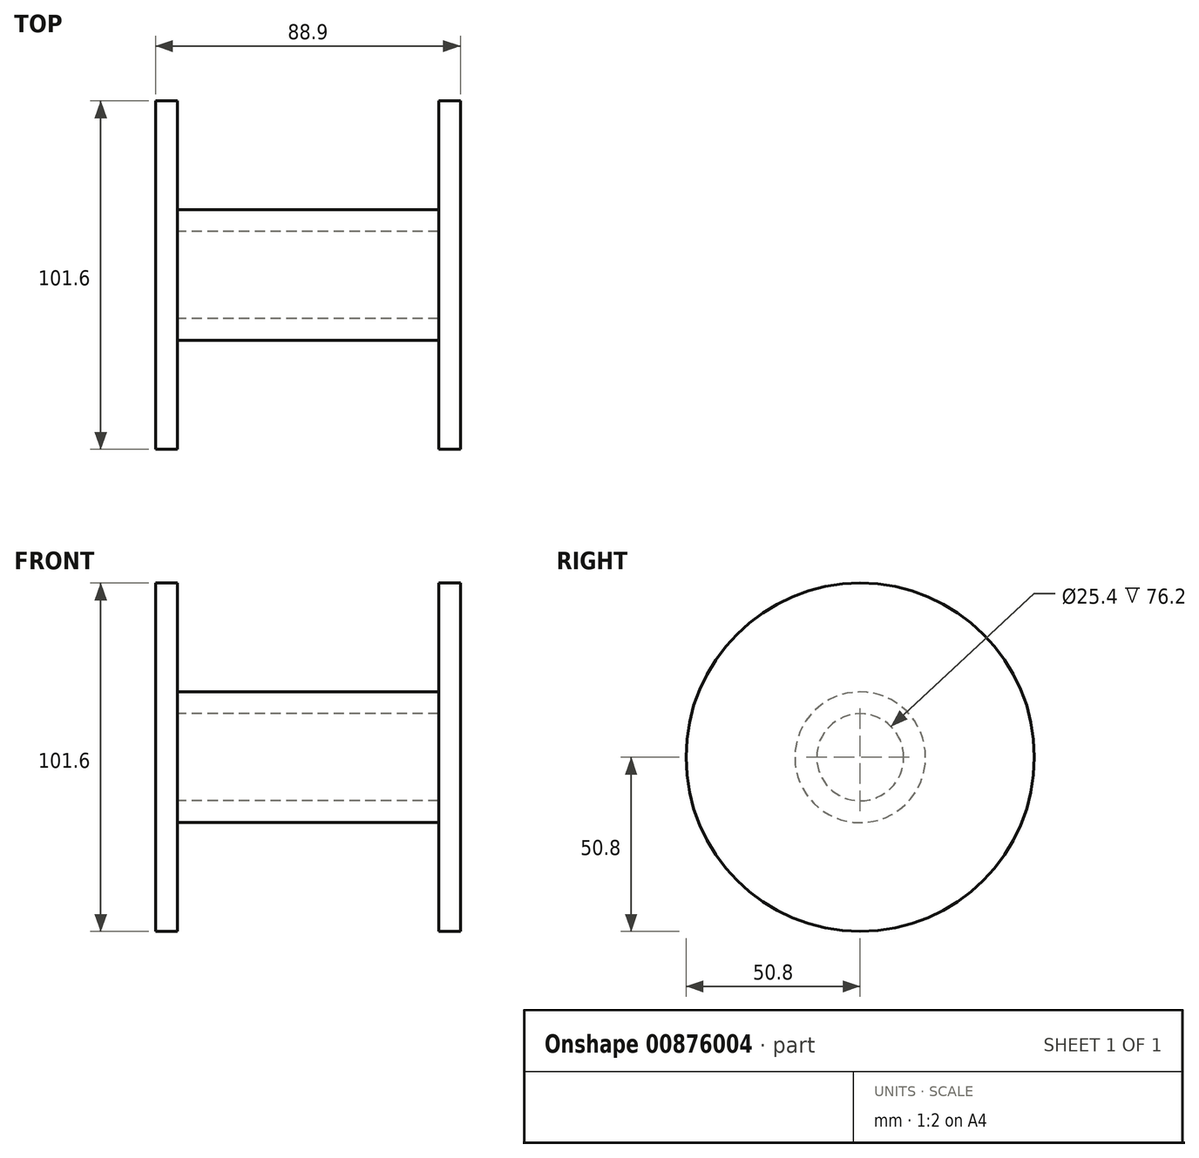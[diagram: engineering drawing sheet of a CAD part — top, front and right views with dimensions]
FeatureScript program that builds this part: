
annotation { "Feature Type Name" : "Feature", "Feature Type Description" : "" }
export const myFeature = defineFeature(function(context is Context, id is Id, definition is map)
    precondition{}
    {
        {
            var Q0;
            Q0=qCreatedBy(makeId("Right.planeOp"),FACE);
            cPlane(context, id + "F0", {"entities" : qUnion([Q0]), "cplaneType" : CPlaneType.OFFSET, "offset" : 38.1 * mm, "width" : 152.4 * mm, "height" : 152.4 * mm});
        }
        {
            var Q0;
            Q0=qCreatedBy(makeId("Right.planeOp"),FACE);
            cPlane(context, id + "F1", {"entities" : qUnion([Q0]), "cplaneType" : CPlaneType.OFFSET, "offset" : 38.1 * mm, "oppositeDirection" : true, "width" : 152.4 * mm, "height" : 152.4 * mm});
        }
        {
            var Q0;
            Q0=qCreatedBy(id+"F1.planeOp",FACE);
            var sketch = newSketch(context, id + "F2", { "sketchPlane" : qUnion([Q0])});
            skCircle(sketch, "E0", {"center": v(0, 0) * mm, "radius": 50.8 * mm});
            skSolve(sketch);
        }
        {
            var Q0;
            Q0=qCreatedBy(id+"F0.planeOp",FACE);
            var sketch = newSketch(context, id + "F3", { "sketchPlane" : qUnion([Q0])});
            skCircle(sketch, "E1", {"center": v(0, 0) * mm, "radius": 50.8 * mm});
            skSolve(sketch);
        }
        {
            var Q0;
            Q0 = qSketchRegion(id + "F2", true);
            extrude(context, id + "F4", {"entities" : qUnion([Q0]), "oppositeDirection" : true, "depth" : 6.35 * mm, "offsetDistance" : 25.4 * mm});
        }
        {
            var Q0;
            Q0=qCreatedBy(makeId("Right.planeOp"),FACE);
            var sketch = newSketch(context, id + "F5", { "sketchPlane" : qUnion([Q0])});
            skCircle(sketch, "E2", {"center": v(0, 0) * mm, "radius": 12.7 * mm});
            skCircle(sketch, "E3.0", {"center": v(0, 0) * mm, "radius": 19.05 * mm});
            skSolve(sketch);
        }
        {
            var Q0;
            Q0 = qSketchRegion(id + "F5", true);
            extrude(context, id + "F6", {"entities" : qUnion([Q0]), "operationType" : NewBodyOperationType.ADD, "endBound" : BoundingType.SYMMETRIC, "depth" : 76.2 * mm, "offsetDistance" : 25.4 * mm});
        }
        {
            var Q0;
            Q0 = qSketchRegion(id + "F3", true);
            var Q1;
            Q1=sQuery(id+"F3.wireOp",EDGE,"E1");
            extrude(context, id + "F7", {"entities" : qUnion([Q0]), "operationType" : NewBodyOperationType.ADD, "surfaceOperationType" : NewSurfaceOperationType.ADD, "surfaceEntities" : qUnion([Q1]), "depth" : 6.35 * mm, "offsetDistance" : 25.4 * mm});
        }
    });
